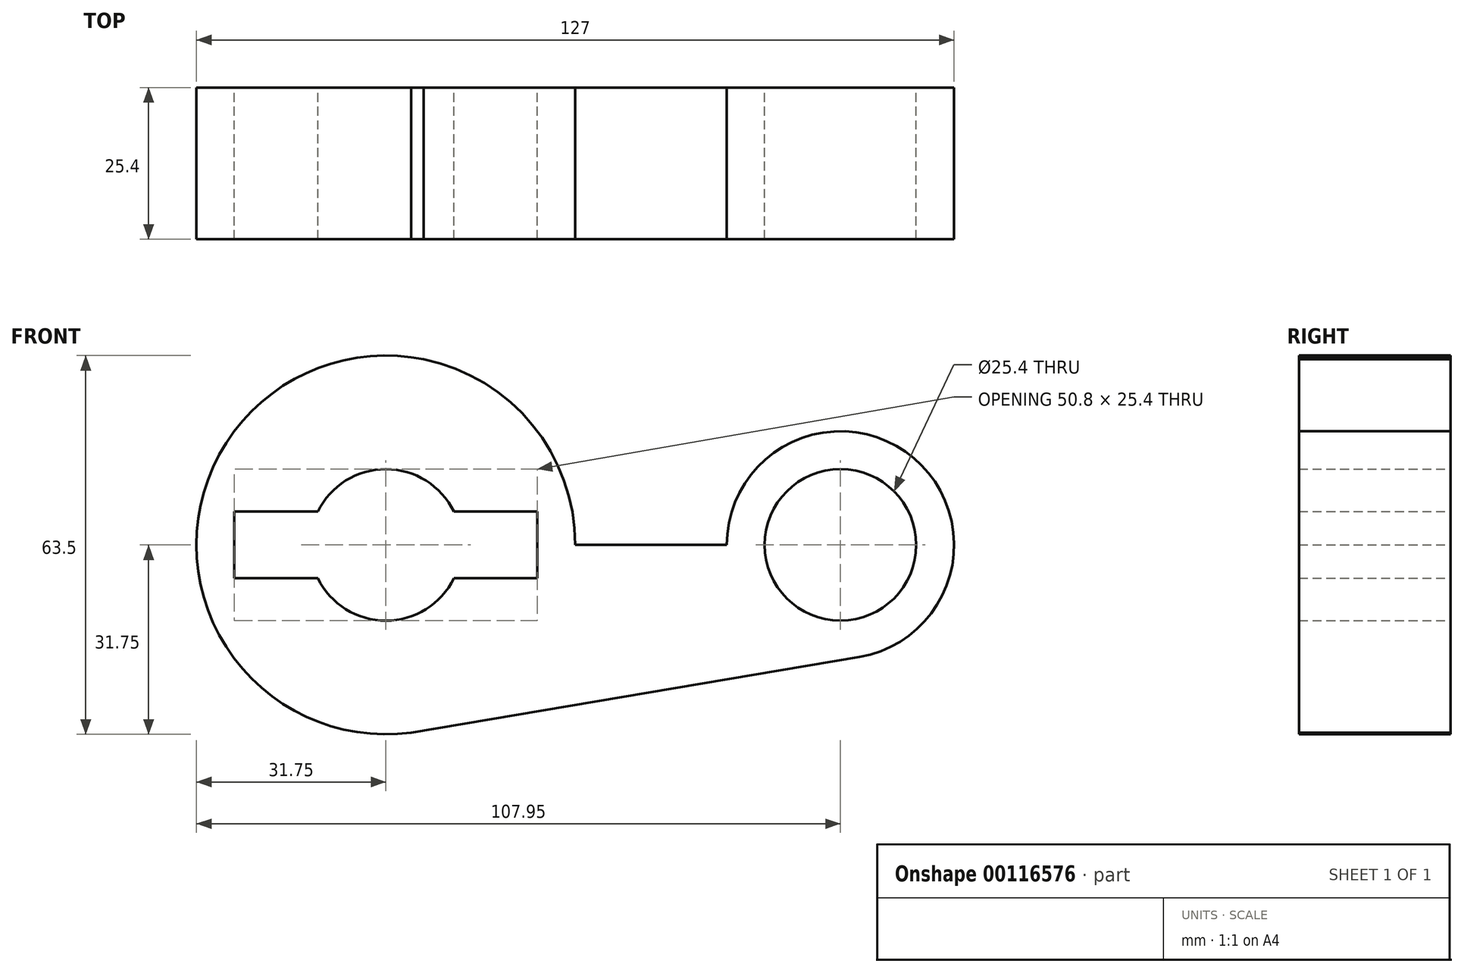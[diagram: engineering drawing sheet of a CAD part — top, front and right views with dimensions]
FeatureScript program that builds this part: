
annotation { "Feature Type Name" : "Feature", "Feature Type Description" : "" }
export const myFeature = defineFeature(function(context is Context, id is Id, definition is map)
    precondition{}
    {
        {
            var Q0;
            Q0=qCreatedBy(makeId("Front.planeOp"),FACE);
            var sketch = newSketch(context, id + "F0", { "sketchPlane" : qUnion([Q0])});
            skCircle(sketch, "E0", {"center": v(0, 0) * mm, "radius": 31.75 * mm});
            skCircle(sketch, "E1", {"center": v(76.2, 0) * mm, "radius": 19.05 * mm});
            skLineSegment(sketch, "E2", {"start": v(4.23, 31.47) * mm, "end": v(79.37, 18.78) * mm});
            skLineSegment(sketch, "E3", {"start": v(4.23, -31.47) * mm, "end": v(79.37, -18.78) * mm});
            skLineSegment(sketch, "E4", {"start": v(0, 0) * mm, "end": v(76.2, 0) * mm});
            skCircle(sketch, "E5", {"center": v(0, 0) * mm, "radius": 12.7 * mm});
            skCircle(sketch, "E6", {"center": v(76.2, 0) * mm, "radius": 12.7 * mm});
            skLineSegment(sketch, "E7.bottom", {"start": v(25.4, -5.59) * mm, "end": v(-25.4, -5.59) * mm});
            skLineSegment(sketch, "E7.top", {"start": v(25.4, 5.59) * mm, "end": v(-25.4, 5.59) * mm});
            skLineSegment(sketch, "E7.left", {"start": v(25.4, -5.59) * mm, "end": v(25.4, 5.59) * mm});
            skLineSegment(sketch, "E7.right", {"start": v(-25.4, -5.59) * mm, "end": v(-25.4, 5.59) * mm});
            skSolve(sketch);
        }
        {
            var Q0;
            {var subQ11=sQuery(id+"F0.wireOp",EDGE,"E7.right");Q0=makeQuery(id+"F0.imprint","IMPRINT",FACE,{"disambiguationData":[TD([[makeQuery(id+"F0.imprint","IMPRINT",EDGE,{"derivedFrom":subQ11}),1.0]])]});}
            var Q1;
            {var subQ0=sQuery(id+"F0.wireOp",EDGE,"E4");var subQ1=sQuery(id+"F0.wireOp",EDGE,"E0");var subQ2=makeQuery(id+"F0.imprint","INTERSECT",VERTEX,{"derivedFrom":[subQ1,subQ0]});Q1=makeQuery(id+"F0.imprint","IMPRINT",FACE,{"disambiguationData":[TD([[makeQuery(id+"F0.imprint","IMPRINT",EDGE,{"disambiguationData":[TD([[subQ2,1.0]])],"derivedFrom":subQ1}),-1.0]])]});}
            var Q2;
            Q2=makeQuery(id+"F0.imprint","IMPRINT",FACE,{"disambiguationData":[TD([[makeQuery(id+"F0.imprint","IMPRINT",EDGE,{"derivedFrom":sQuery(id+"F0.wireOp",EDGE,"E6")}),-1.0]])]});
            var Q3;
            {var subQ0=sQuery(id+"F0.wireOp",EDGE,"E2");var subQ1=sQuery(id+"F0.wireOp",EDGE,"E0");var subQ2=makeQuery(id+"F0.imprint","INTERSECT",VERTEX,{"disambiguationData":[OD(1.0)],"derivedFrom":[subQ1,subQ0]});Q3=makeQuery(id+"F0.imprint","IMPRINT",FACE,{"disambiguationData":[TD([[makeQuery(id+"F0.imprint","IMPRINT",EDGE,{"disambiguationData":[TD([[subQ2,1.0]])],"derivedFrom":subQ1}),-1.0]])]});}
            extrude(context, id + "F1", {"entities" : qUnion([Q0, Q1, Q2, Q3]), "depth" : 25.4 * mm});
        }
    });
